# Revit family: Haworth_Aloha_Easy_Chair_Guest_AP_PRELIMINARY
name_source: partatom
category: Furniture
units: mm (PartAtom-declared; Revit-internal decimal feet)

## family parameters
Always vertical = Yes
Cut with Voids When Loaded = No
OmniClass Number = 23.40.70.14.64.11
OmniClass Title = Office Furniture
Room Calculation Point = No
Shared = No
Work Plane-Based = No

## types (3) — shared parameters
Arm Cap Finish = Haworth _ Polymer _ Black
Assembly Code = E2020200
Caster Finish = Haworth _ Polymer _ Black
Depth = 559 mm
Description = Haworth - Aloha Easy - Guest
Fabric Back = Yes
Manufacturer = Haworth
Model = SE65RGXM1
Revision Number = 1
Size = Verify Final Dim. w/Haworth
Solid Back = No
URL = https://www.haworth.com
URL - Product = https://www.haworth.com
Warranty = http://www.haworth.com
Width = 559 mm

## per-type parameters (varying)
| type | Casters | Four Legs | Glides | Sled Base | Without Casters |
| Sled Base | No | No | Yes | Yes | No |
| Four Legs w Casters | Yes | Yes | No | No | No |
| Four Legs w Glides | No | Yes | No | No | Yes |

## geometry (parser evidence)
native form markers: Blend x4, Sweep x5
no freeform markers — native parametric forms only
